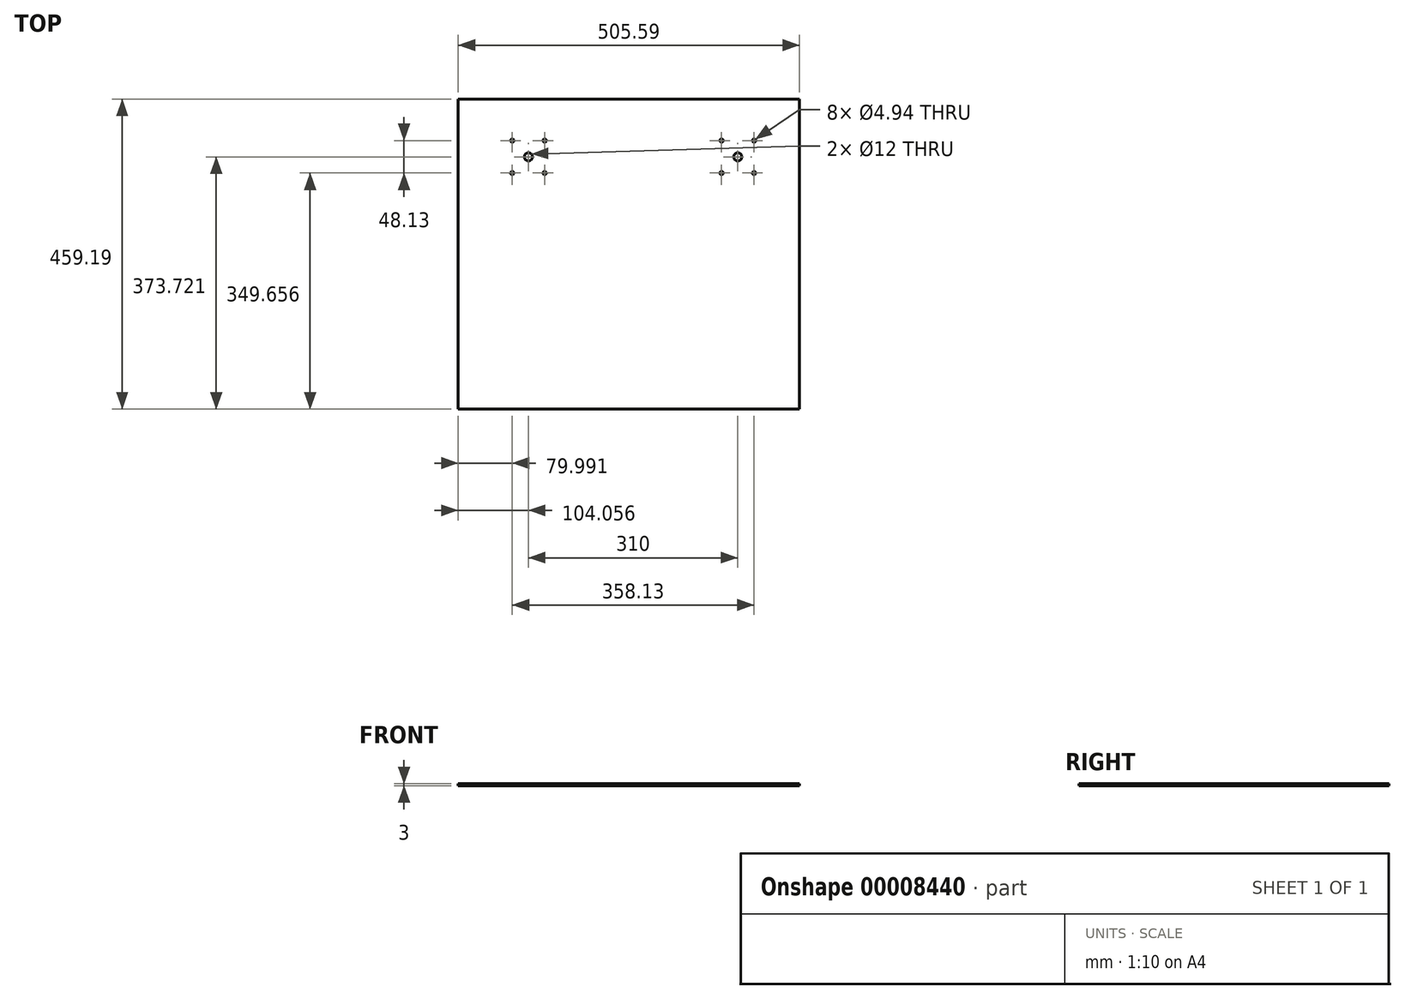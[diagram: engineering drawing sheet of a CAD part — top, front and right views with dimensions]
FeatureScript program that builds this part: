
annotation { "Feature Type Name" : "Feature", "Feature Type Description" : "" }
export const myFeature = defineFeature(function(context is Context, id is Id, definition is map)
    precondition{}
    {
        {
            var Q0;
            Q0=qCreatedBy(makeId("Top.planeOp"),FACE);
            var sketch = newSketch(context, id + "F0", { "sketchPlane" : qUnion([Q0])});
            skCircle(sketch, "E0", {"center": v(-27.08, 27.3) * mm, "radius": 2.47 * mm});
            skCircle(sketch, "E1", {"center": v(21.05, 27.3) * mm, "radius": 2.47 * mm});
            skCircle(sketch, "E2", {"center": v(21.05, -20.82) * mm, "radius": 2.47 * mm});
            skCircle(sketch, "E3", {"center": v(-27.08, -20.82) * mm, "radius": 2.47 * mm});
            skCircle(sketch, "E4", {"center": v(331.05, 27.3) * mm, "radius": 2.47 * mm});
            skCircle(sketch, "E5", {"center": v(282.92, 27.3) * mm, "radius": 2.47 * mm});
            skCircle(sketch, "E6", {"center": v(282.92, -20.82) * mm, "radius": 2.47 * mm});
            skCircle(sketch, "E7", {"center": v(331.05, -20.82) * mm, "radius": 2.47 * mm});
            skLineSegment(sketch, "E8", {"start": v(-27.08, 27.3) * mm, "end": v(21.05, 27.3) * mm, "construction": true});
            skLineSegment(sketch, "E9", {"start": v(282.92, 27.3) * mm, "end": v(331.05, 27.3) * mm, "construction": true});
            skLineSegment(sketch, "E10", {"start": v(-27.08, 27.3) * mm, "end": v(-27.08, -20.82) * mm, "construction": true});
            skPoint(sketch, "E11", {"position": v(-3.01, 27.3) * mm});
            skPoint(sketch, "E12", {"position": v(-27.08, 3.24) * mm});
            skPoint(sketch, "E13", {"position": v(306.99, 27.3) * mm});
            skPoint(sketch, "E14", {"position": v(306.99, 3.24) * mm});
            skPoint(sketch, "E15", {"position": v(-3.01, 3.24) * mm});
            skCircle(sketch, "E16", {"center": v(-3.01, 3.24) * mm, "radius": 6 * mm});
            skCircle(sketch, "E17", {"center": v(306.99, 3.24) * mm, "radius": 6 * mm});
            skLineSegment(sketch, "E18.bottom", {"start": v(-107.07, 88.71) * mm, "end": v(398.52, 88.71) * mm});
            skLineSegment(sketch, "E18.top", {"start": v(-107.07, -370.48) * mm, "end": v(398.52, -370.48) * mm});
            skLineSegment(sketch, "E18.left", {"start": v(-107.07, 88.71) * mm, "end": v(-107.07, -370.48) * mm});
            skLineSegment(sketch, "E18.right", {"start": v(398.52, 88.71) * mm, "end": v(398.52, -370.48) * mm});
            skSolve(sketch);
        }
        {
            var Q0;
            Q0=makeQuery(id+"F0.imprint","IMPRINT",FACE,{"disambiguationData":[TD([[makeQuery(id+"F0.imprint","IMPRINT",EDGE,{"derivedFrom":sQuery(id+"F0.wireOp",EDGE,"E0")}),-1.0]])]});
            extrude(context, id + "F1", {"entities" : qUnion([Q0]), "depth" : 3 * mm});
        }
    });
